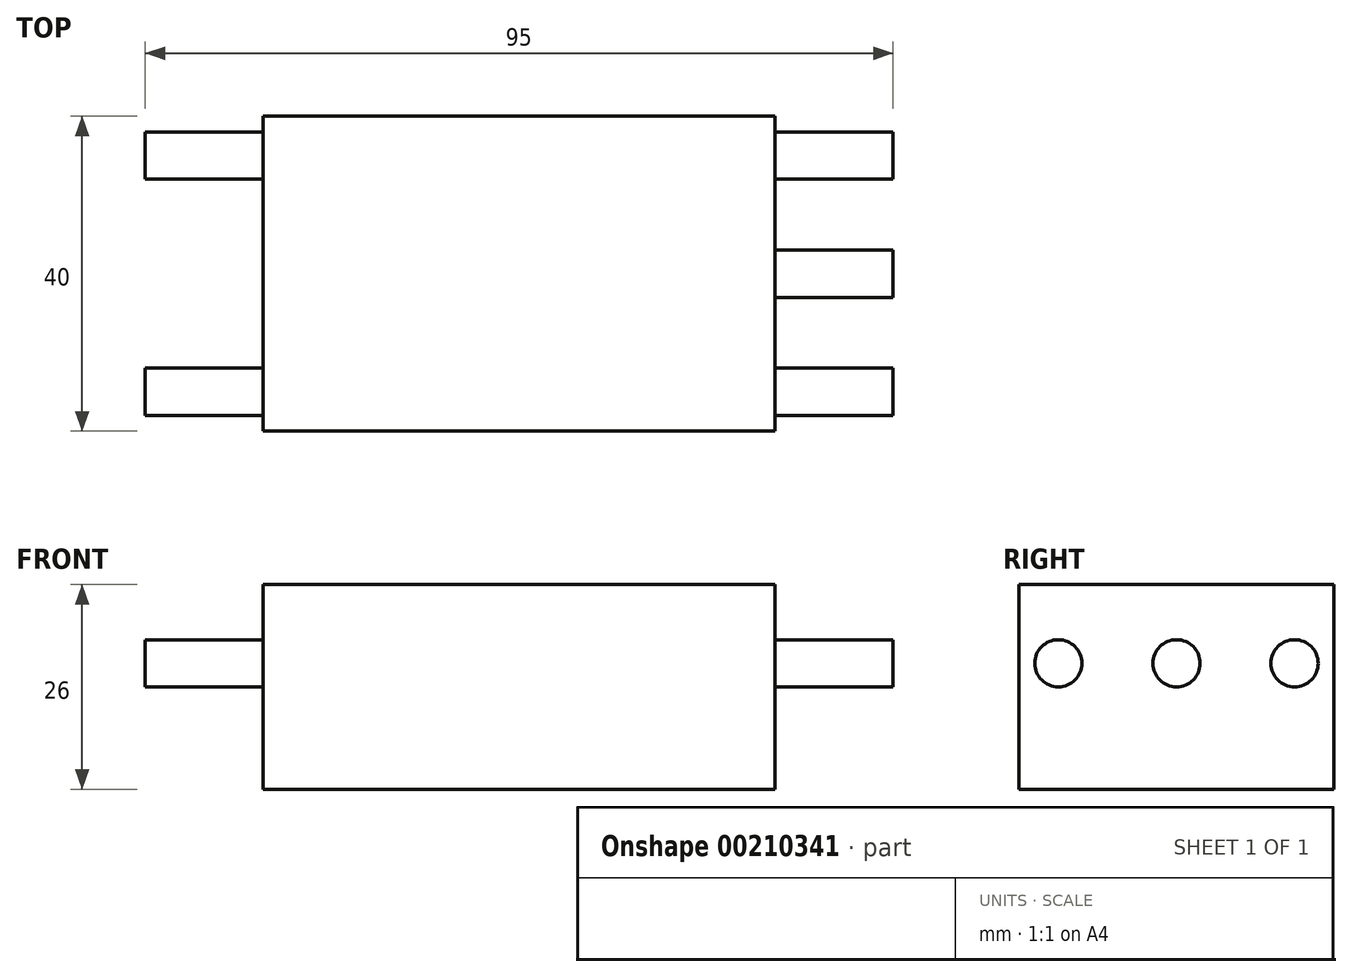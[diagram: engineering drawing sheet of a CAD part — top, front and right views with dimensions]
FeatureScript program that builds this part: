
annotation { "Feature Type Name" : "Feature", "Feature Type Description" : "" }
export const myFeature = defineFeature(function(context is Context, id is Id, definition is map)
    precondition{}
    {
        {
            var Q0;
            Q0=qCreatedBy(makeId("Top.planeOp"),FACE);
            var sketch = newSketch(context, id + "F0", { "sketchPlane" : qUnion([Q0])});
            skLineSegment(sketch, "E0.bottom", {"start": v(-32.5, 20) * mm, "end": v(32.5, 20) * mm});
            skLineSegment(sketch, "E0.top", {"start": v(-32.5, -20) * mm, "end": v(32.5, -20) * mm});
            skLineSegment(sketch, "E0.left", {"start": v(-32.5, 20) * mm, "end": v(-32.5, -20) * mm});
            skLineSegment(sketch, "E0.right", {"start": v(32.5, 20) * mm, "end": v(32.5, -20) * mm});
            skSolve(sketch);
        }
        {
            var Q0;
            Q0 = qSketchRegion(id + "F0", true);
            extrude(context, id + "F1", {"entities" : qUnion([Q0]), "depth" : 26 * mm});
        }
        {
            var Q0;
            Q0=makeQuery(id+"F1.opExtrude","SWEPT_FACE",FACE,{"disambiguationData":[OSD([sQuery(id+"F0.wireOp",EDGE,"E0.right")])]});
            var sketch = newSketch(context, id + "F2", { "sketchPlane" : qUnion([Q0])});
            skLineSegment(sketch, "E1", {"start": v(-40.68, 16) * mm, "end": v(43.17, 16) * mm, "construction": true});
            skCircle(sketch, "E2", {"center": v(0, 16) * mm, "radius": 3 * mm});
            skCircle(sketch, "E3", {"center": v(-15, 16) * mm, "radius": 3 * mm});
            skCircle(sketch, "E4", {"center": v(15, 16) * mm, "radius": 3 * mm});
            skSolve(sketch);
        }
        {
            var Q0;
            Q0 = qSketchRegion(id + "F2", true);
            extrude(context, id + "F3", {"entities" : qUnion([Q0]), "operationType" : NewBodyOperationType.ADD, "depth" : 15 * mm});
        }
        {
            var Q0;
            Q0=makeQuery(id+"F1.opExtrude","SWEPT_FACE",FACE,{"disambiguationData":[OSD([sQuery(id+"F0.wireOp",EDGE,"E0.left")])]});
            var sketch = newSketch(context, id + "F4", { "sketchPlane" : qUnion([Q0])});
            skLineSegment(sketch, "E5", {"start": v(-57.42, 16) * mm, "end": v(58.44, 16) * mm, "construction": true});
            skCircle(sketch, "E6", {"center": v(15, 16) * mm, "radius": 3 * mm});
            skCircle(sketch, "E7", {"center": v(-15, 16) * mm, "radius": 3 * mm});
            skSolve(sketch);
        }
        {
            var Q0;
            Q0 = qSketchRegion(id + "F4", true);
            extrude(context, id + "F5", {"entities" : qUnion([Q0]), "operationType" : NewBodyOperationType.ADD, "depth" : 15 * mm});
        }
    });
